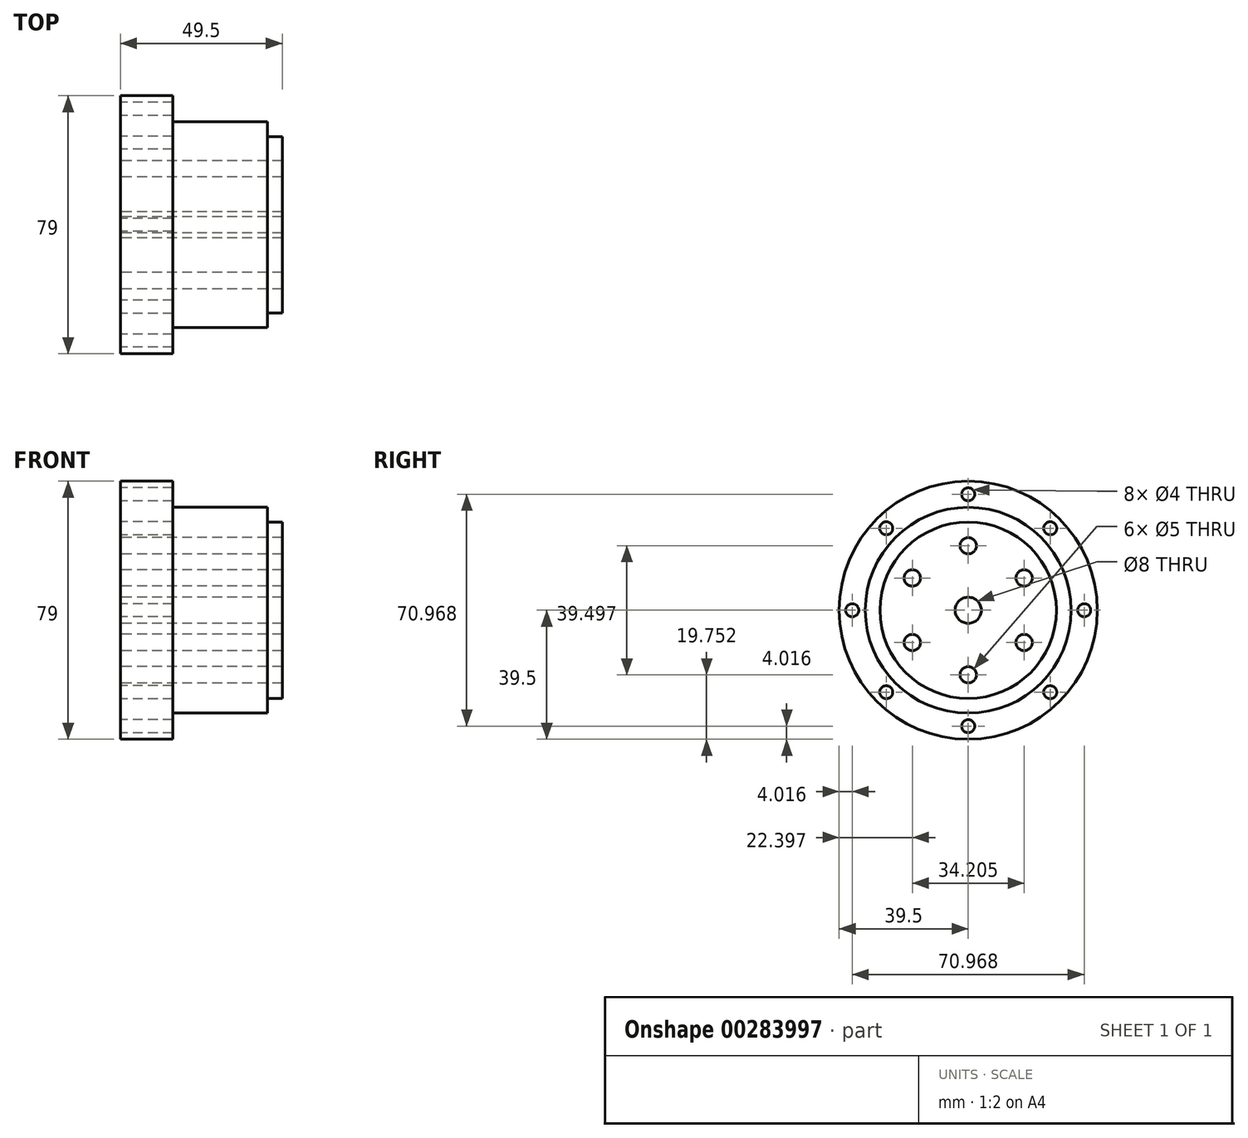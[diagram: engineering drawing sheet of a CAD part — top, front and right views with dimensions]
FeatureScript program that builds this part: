
annotation { "Feature Type Name" : "Feature", "Feature Type Description" : "" }
export const myFeature = defineFeature(function(context is Context, id is Id, definition is map)
    precondition{}
    {
        {
            var Q0;
            Q0=qCreatedBy(makeId("Right.planeOp"),FACE);
            var sketch = newSketch(context, id + "F0", { "sketchPlane" : qUnion([Q0])});
            skCircle(sketch, "E0", {"center": v(0, 0) * mm, "radius": 39.5 * mm});
            skCircle(sketch, "E1", {"center": v(0, 0) * mm, "radius": 31.5 * mm});
            skCircle(sketch, "E2", {"center": v(0, 0) * mm, "radius": 4 * mm});
            skCircle(sketch, "E3", {"center": v(0, 19.75) * mm, "radius": 2.5 * mm});
            skCircle(sketch, "E4.1.0", {"center": v(-17.1, 9.87) * mm, "radius": 2.5 * mm});
            skCircle(sketch, "E4.2.0", {"center": v(-17.1, -9.87) * mm, "radius": 2.5 * mm});
            skCircle(sketch, "E4.3.0", {"center": v(0, -19.75) * mm, "radius": 2.5 * mm});
            skCircle(sketch, "E4.4.0", {"center": v(17.1, -9.87) * mm, "radius": 2.5 * mm});
            skCircle(sketch, "E4.5.0", {"center": v(17.1, 9.87) * mm, "radius": 2.5 * mm});
            skCircle(sketch, "E5", {"center": v(0, 35.48) * mm, "radius": 2 * mm});
            skCircle(sketch, "E6.1.0", {"center": v(-25.1, 25.1) * mm, "radius": 2 * mm});
            skCircle(sketch, "E6.2.0", {"center": v(-35.48, 0) * mm, "radius": 2 * mm});
            skCircle(sketch, "E6.3.0", {"center": v(-25.1, -25.1) * mm, "radius": 2 * mm});
            skCircle(sketch, "E6.4.0", {"center": v(0, -35.48) * mm, "radius": 2 * mm});
            skCircle(sketch, "E6.5.0", {"center": v(25.1, -25.1) * mm, "radius": 2 * mm});
            skCircle(sketch, "E6.6.0", {"center": v(35.48, 0) * mm, "radius": 2 * mm});
            skCircle(sketch, "E6.7.0", {"center": v(25.1, 25.1) * mm, "radius": 2 * mm});
            skCircle(sketch, "E7", {"center": v(0, 0) * mm, "radius": 26.99 * mm});
            skSolve(sketch);
        }
        {
            var Q0;
            Q0=makeQuery(id+"F0.imprint","IMPRINT",FACE,{"disambiguationData":[TD([[makeQuery(id+"F0.imprint","IMPRINT",EDGE,{"derivedFrom":sQuery(id+"F0.wireOp",EDGE,"E1")}),1.0]])]});
            extrude(context, id + "F1", {"entities" : qUnion([Q0]), "depth" : 45 * mm});
        }
        {
            var Q0;
            Q0=makeQuery(id+"F0.imprint","IMPRINT",FACE,{"disambiguationData":[TD([[makeQuery(id+"F0.imprint","IMPRINT",EDGE,{"derivedFrom":sQuery(id+"F0.wireOp",EDGE,"E0")}),1.0]])]});
            extrude(context, id + "F2", {"entities" : qUnion([Q0]), "operationType" : NewBodyOperationType.ADD, "depth" : 16 * mm});
        }
        {
            var Q0;
            Q0=makeQuery(id+"F0.imprint","IMPRINT",FACE,{"disambiguationData":[TD([[makeQuery(id+"F0.imprint","IMPRINT",EDGE,{"derivedFrom":sQuery(id+"F0.wireOp",EDGE,"E2")}),-1.0]])]});
            extrude(context, id + "F3", {"entities" : qUnion([Q0]), "operationType" : NewBodyOperationType.ADD, "depth" : 45 * mm + 4.5 * mm});
        }
    });
